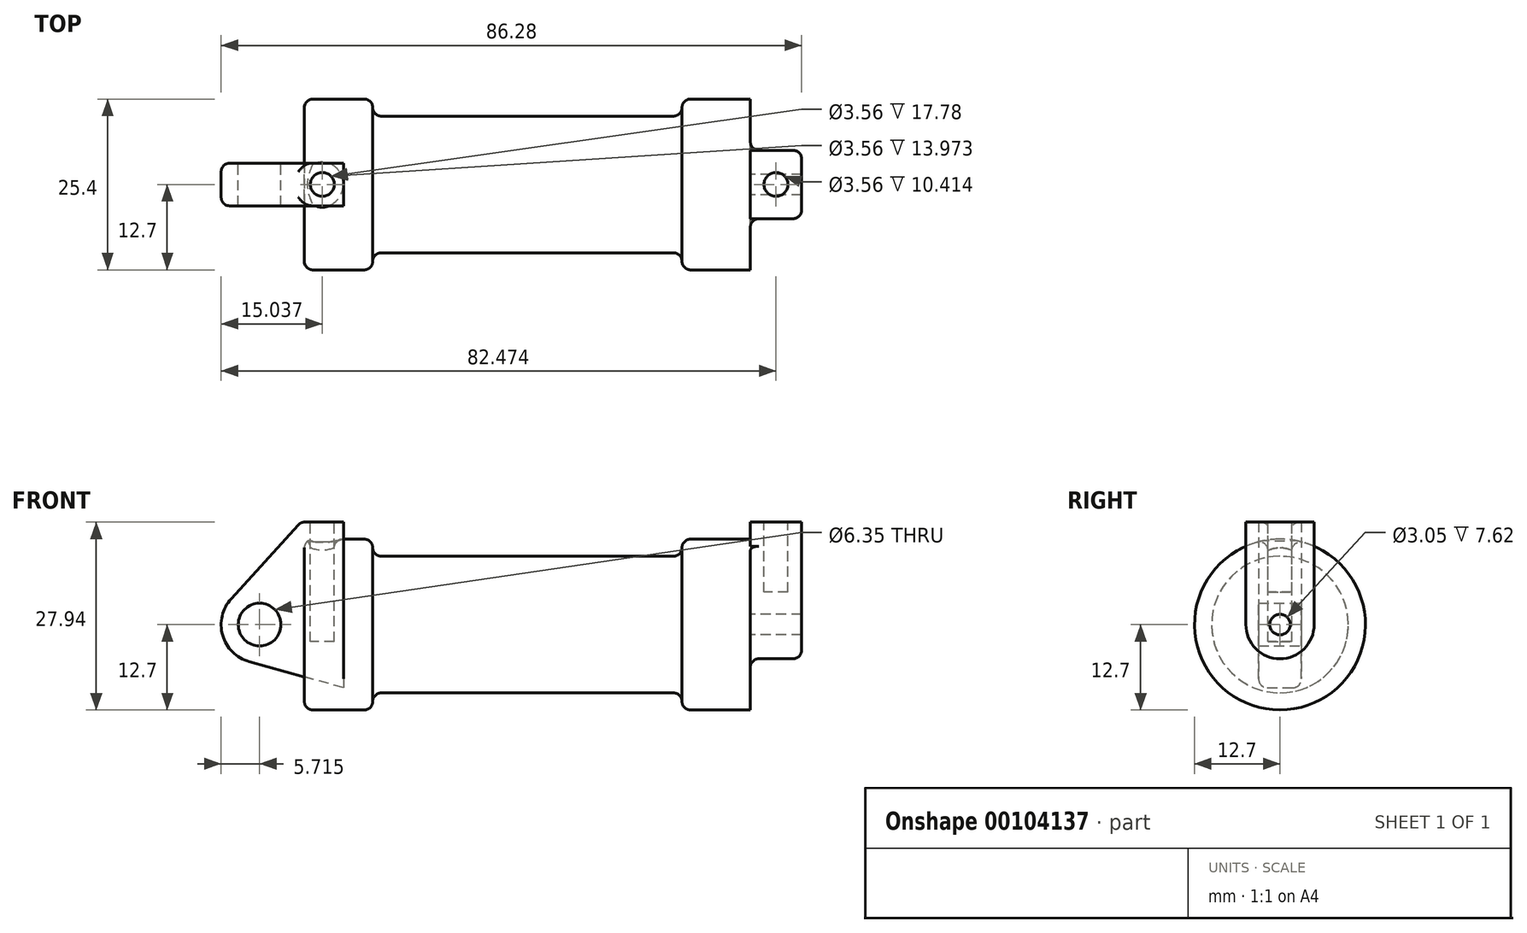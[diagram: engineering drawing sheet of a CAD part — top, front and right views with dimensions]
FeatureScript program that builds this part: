
annotation { "Feature Type Name" : "Feature", "Feature Type Description" : "" }
export const myFeature = defineFeature(function(context is Context, id is Id, definition is map)
    precondition{}
    {
        {
            var Q0;
            Q0=qCreatedBy(makeId("Front.planeOp"),FACE);
            var sketch = newSketch(context, id + "F0", { "sketchPlane" : qUnion([Q0])});
            skLineSegment(sketch, "E0", {"start": v(0, 0) * mm, "end": v(0, 12.7) * mm});
            skLineSegment(sketch, "E1", {"start": v(0, 12.7) * mm, "end": v(10.16, 12.7) * mm});
            skLineSegment(sketch, "E2", {"start": v(10.16, 12.7) * mm, "end": v(10.16, 10.16) * mm});
            skLineSegment(sketch, "E3", {"start": v(10.16, 10.16) * mm, "end": v(56.13, 10.16) * mm});
            skLineSegment(sketch, "E4", {"start": v(56.13, 10.16) * mm, "end": v(56.13, 12.7) * mm});
            skLineSegment(sketch, "E5", {"start": v(56.13, 12.7) * mm, "end": v(66.3, 12.7) * mm});
            skLineSegment(sketch, "E6", {"start": v(66.3, 12.7) * mm, "end": v(66.3, 0) * mm});
            skLineSegment(sketch, "E7", {"start": v(66.3, 0) * mm, "end": v(0, 0) * mm});
            skLineSegment(sketch, "E8", {"start": v(5.84, 15.24) * mm, "end": v(-0.5, 15.24) * mm});
            skLineSegment(sketch, "E9", {"start": v(-0.5, 15.24) * mm, "end": v(-10.88, 3.85) * mm});
            skLineSegment(sketch, "E10", {"start": v(0, 0) * mm, "end": v(-6.65, 0) * mm});
            skCircle(sketch, "E11", {"center": v(-6.65, 0) * mm, "radius": 5.72 * mm});
            skCircle(sketch, "E12", {"center": v(-6.65, 0) * mm, "radius": 3.18 * mm});
            skLineSegment(sketch, "E13", {"start": v(5.84, 15.24) * mm, "end": v(5.84, -9.4) * mm});
            skLineSegment(sketch, "E14", {"start": v(5.84, -9.4) * mm, "end": v(-8.18, -5.5) * mm});
            skSolve(sketch);
        }
        {
            var Q0;
            {var subQ0=sQuery(id+"F0.wireOp",EDGE,"E2");Q0=makeQuery(id+"F0.imprint","IMPRINT",FACE,{"disambiguationData":[TD([[makeQuery(id+"F0.imprint","IMPRINT",EDGE,{"derivedFrom":subQ0}),-1.0]])]});}
            var Q1;
            {var subQ0=sQuery(id+"F0.wireOp",EDGE,"E0");Q1=makeQuery(id+"F0.imprint","IMPRINT",FACE,{"disambiguationData":[TD([[makeQuery(id+"F0.imprint","IMPRINT",EDGE,{"derivedFrom":subQ0}),-1.0]])]});}
            var Q2;
            Q2=sQuery(id+"F0.wireOp",EDGE,"E7");
            revolve(context, id + "F1", {"entities" : qUnion([Q0, Q1]), "axis" : qUnion([Q2]), "revolveType" : RevolveType.FULL});
        }
        {
            var Q0;
            {var subQ0=sQuery(id+"F0.wireOp",EDGE,"E14");Q0=makeQuery(id+"F0.imprint","IMPRINT",FACE,{"disambiguationData":[TD([[makeQuery(id+"F0.imprint","IMPRINT",EDGE,{"derivedFrom":subQ0}),-1.0]])]});}
            var Q1;
            {var subQ0=sQuery(id+"F0.wireOp",EDGE,"E0");Q1=makeQuery(id+"F0.imprint","IMPRINT",FACE,{"disambiguationData":[TD([[makeQuery(id+"F0.imprint","IMPRINT",EDGE,{"derivedFrom":subQ0}),-1.0]])]});}
            var Q2;
            {var subQ3=sQuery(id+"F0.wireOp",EDGE,"E0");Q2=makeQuery(id+"F0.imprint","IMPRINT",FACE,{"disambiguationData":[TD([[makeQuery(id+"F0.imprint","IMPRINT",EDGE,{"derivedFrom":subQ3}),1.0]])]});}
            var Q3;
            {var subQ4=sQuery(id+"F0.wireOp",EDGE,"E12");Q3=makeQuery(id+"F0.imprint","IMPRINT",FACE,{"disambiguationData":[TD([[makeQuery(id+"F0.imprint","IMPRINT",EDGE,{"derivedFrom":subQ4}),-1.0]])]});}
            extrude(context, id + "F2", {"entities" : qUnion([Q0, Q1, Q2, Q3]), "endBound" : BoundingType.SYMMETRIC, "depth" : 6.35 * mm});
        }
        {
            var Q0;
            Q0=makeQuery(id+"F1.opRevolve","SWEPT_FACE",FACE,{"disambiguationData":[OSD([sQuery(id+"F0.wireOp",EDGE,"E6")])]});
            var sketch = newSketch(context, id + "F3", { "sketchPlane" : qUnion([Q0])});
            skCircle(sketch, "E15", {"center": v(0, 0) * mm, "radius": 5.08 * mm});
            skLineSegment(sketch, "E16", {"start": v(-5.08, 0) * mm, "end": v(-5.08, 15.24) * mm});
            skLineSegment(sketch, "E17.MirrorCS", {"start": v(5.08, 0) * mm, "end": v(5.08, 15.24) * mm});
            skCircle(sketch, "E18", {"center": v(0, 0) * mm, "radius": 1.52 * mm});
            skLineSegment(sketch, "E19", {"start": v(-5.08, 15.24) * mm, "end": v(5.08, 15.24) * mm});
            skSolve(sketch);
        }
        {
            var Q0;
            Q0=makeQuery(id+"F3.imprint","IMPRINT",FACE,{"disambiguationData":[TD([[makeQuery(id+"F3.imprint","IMPRINT",EDGE,{"derivedFrom":sQuery(id+"F3.wireOp",EDGE,"E18")}),-1.0]])]});
            var Q1;
            {var subQ0=sQuery(id+"F3.wireOp",EDGE,"E16");var subQ1=sQuery(id+"F3.wireOp",EDGE,"E15");var subQ2=makeQuery(id+"F3.imprint","INTERSECT",VERTEX,{"derivedFrom":[subQ1,subQ0]});Q1=makeQuery(id+"F3.imprint","IMPRINT",FACE,{"disambiguationData":[TD([[makeQuery(id+"F3.imprint","IMPRINT",EDGE,{"disambiguationData":[TD([[subQ2,1.0]])],"derivedFrom":subQ1}),-1.0]])]});}
            var Q2;
            {var subQ0=sQuery(id+"F3.wireOp",EDGE,"E19");Q2=makeQuery(id+"F3.imprint","IMPRINT",FACE,{"disambiguationData":[TD([[makeQuery(id+"F3.imprint","IMPRINT",EDGE,{"derivedFrom":subQ0}),-1.0]])]});}
            extrude(context, id + "F4", {"entities" : qUnion([Q0, Q1, Q2]), "operationType" : NewBodyOperationType.ADD, "depth" : 7.62 * mm});
        }
        {
            var Q0;
            Q0=makeQuery(id+"F2.opExtrude","SWEPT_FACE",FACE,{"disambiguationData":[OSD([sQuery(id+"F0.wireOp",EDGE,"E8")])]});
            var sketch = newSketch(context, id + "F5", { "sketchPlane" : qUnion([Q0])});
            skCircle(sketch, "E20", {"center": v(2.67, 0) * mm, "radius": 1.78 * mm});
            skSolve(sketch);
        }
        {
            var Q0;
            Q0=makeQuery(id+"F4.opExtrude","SWEPT_FACE",FACE,{"disambiguationData":[OSD([sQuery(id+"F3.wireOp",EDGE,"E19")])]});
            var sketch = newSketch(context, id + "F6", { "sketchPlane" : qUnion([Q0])});
            skCircle(sketch, "E21", {"center": v(70.1, 0) * mm, "radius": 1.78 * mm});
            skPoint(sketch, "E21.centerSnap0", {"position": v(66.3, 0) * mm});
            skSolve(sketch);
        }
        {
            var Q0;
            Q0=makeQuery(id+"F5.imprint","IMPRINT",FACE,{"disambiguationData":[TD([[makeQuery(id+"F5.imprint","IMPRINT",EDGE,{"derivedFrom":sQuery(id+"F5.wireOp",EDGE,"E20")}),1.0]])]});
            extrude(context, id + "F7", {"entities" : qUnion([Q0]), "operationType" : NewBodyOperationType.REMOVE, "oppositeDirection" : true, "depth" : 17.78 * mm});
        }
        {
            var Q0;
            Q0=makeQuery(id+"F6.imprint","IMPRINT",FACE,{"disambiguationData":[TD([[makeQuery(id+"F6.imprint","IMPRINT",EDGE,{"derivedFrom":sQuery(id+"F6.wireOp",EDGE,"E21")}),1.0]])]});
            extrude(context, id + "F8", {"entities" : qUnion([Q0]), "operationType" : NewBodyOperationType.REMOVE, "oppositeDirection" : true, "depth" : 10.4 * mm});
        }
        {
            var Q0;
            Q0=makeQuery(id+"F1.opRevolve","SWEPT_FACE",FACE,{"disambiguationData":[OSD([sQuery(id+"F0.wireOp",EDGE,"E1")])]});
            var Q1;
            Q1=makeQuery(id+"F1.opRevolve","SWEPT_FACE",FACE,{"disambiguationData":[OSD([sQuery(id+"F0.wireOp",EDGE,"E4")])]});
            var Q2;
            Q2=makeQuery(id+"F2.opExtrude","SWEPT_FACE",FACE,{"disambiguationData":[OSD([sQuery(id+"F0.wireOp",EDGE,"E9")])]});
            fillet(context, id + "F9", {"entities" : qUnion([Q0, Q1, Q2]), "radius" : 1.27 * mm, "tangentPropagation" : true, "allowEdgeOverflow" : false});
        }
        {
            var Q0;
            Q0=makeQuery(id+"F1.opRevolve","SWEPT_FACE",FACE,{"disambiguationData":[OSD([sQuery(id+"F0.wireOp",EDGE,"E3")])]});
            var Q1;
            Q1=makeQuery(id+"F4.opExtrude","SWEPT_FACE",FACE,{"disambiguationData":[OSD([sQuery(id+"F3.wireOp",EDGE,"E15")])]});
            fillet(context, id + "F10", {"entities" : qUnion([Q0, Q1]), "radius" : 1.27 * mm, "tangentPropagation" : true, "allowEdgeOverflow" : false});
        }
    });
